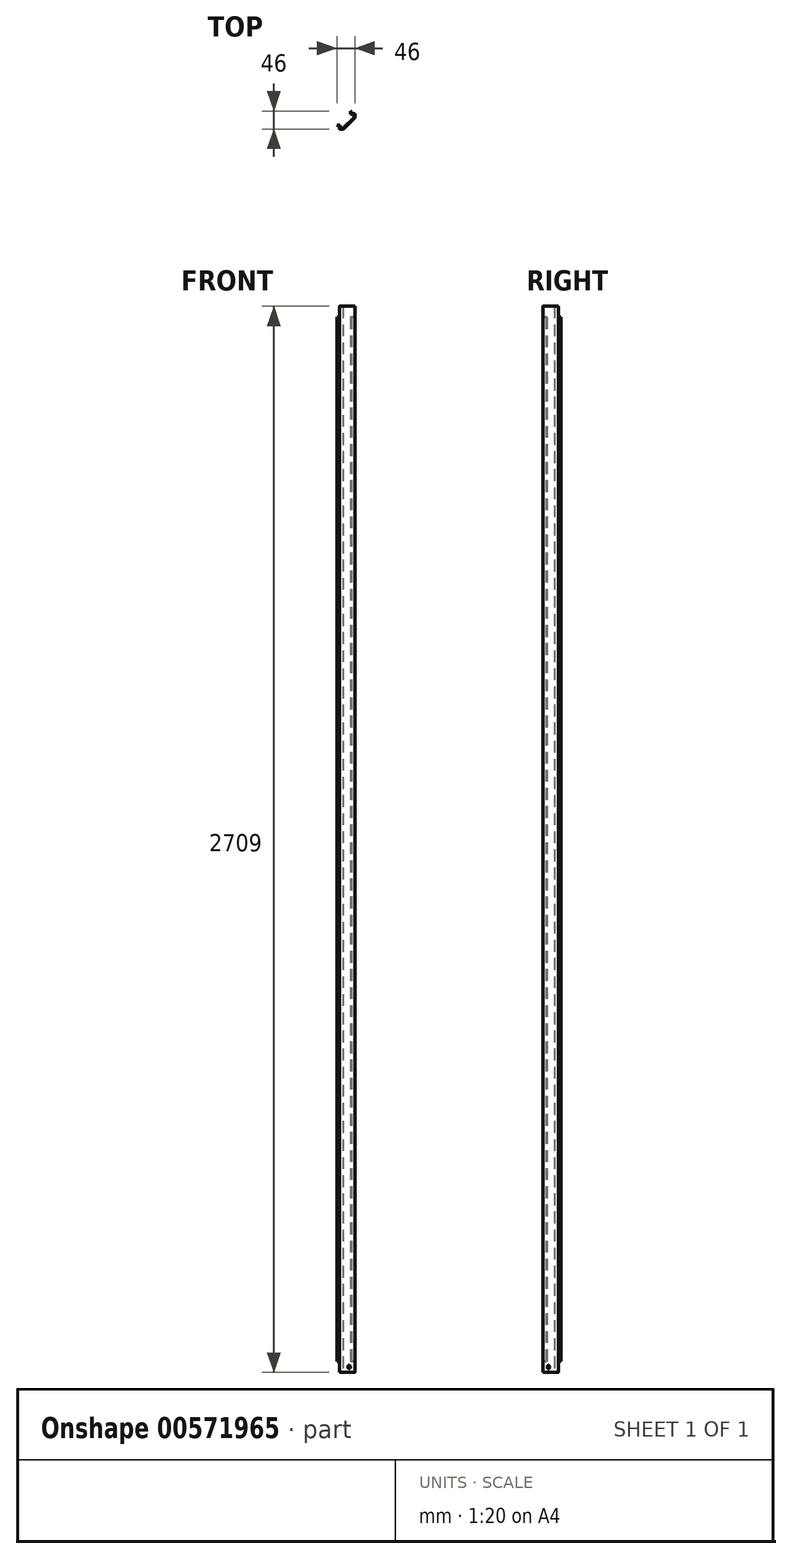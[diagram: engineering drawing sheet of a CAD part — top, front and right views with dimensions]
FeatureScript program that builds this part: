
annotation { "Feature Type Name" : "Feature", "Feature Type Description" : "" }
export const myFeature = defineFeature(function(context is Context, id is Id, definition is map)
    precondition{}
    {
        {
            var Q0;
            Q0=qCreatedBy(makeId("Top.planeOp"),FACE);
            var sketch = newSketch(context, id + "F0", { "sketchPlane" : qUnion([Q0])});
            skLineSegment(sketch, "E0", {"start": v(-68.1, 0) * mm, "end": v(72.16, 0) * mm, "construction": true});
            skLineSegment(sketch, "E1", {"start": v(0, 70.28) * mm, "end": v(0, -61.88) * mm, "construction": true});
            skLineSegment(sketch, "E2.bottom", {"start": v(-19.75, 19.75) * mm, "end": v(19.75, 19.75) * mm, "construction": true});
            skLineSegment(sketch, "E2.top", {"start": v(-19.75, -19.75) * mm, "end": v(19.75, -19.75) * mm, "construction": true});
            skLineSegment(sketch, "E2.left", {"start": v(-19.75, 19.75) * mm, "end": v(-19.75, -19.75) * mm, "construction": true});
            skLineSegment(sketch, "E2.right", {"start": v(19.75, 19.75) * mm, "end": v(19.75, -19.75) * mm, "construction": true});
            skLineSegment(sketch, "E3", {"start": v(-19.75, -19.75) * mm, "end": v(-9.25, -19.75) * mm});
            skLineSegment(sketch, "E4", {"start": v(19.75, 19.75) * mm, "end": v(19.75, 9.25) * mm});
            skLineSegment(sketch, "E5", {"start": v(-9.25, -19.75) * mm, "end": v(19.75, 9.25) * mm});
            skLineSegment(sketch, "E6.0", {"start": v(-19.75, -17.75) * mm, "end": v(-10.08, -17.75) * mm});
            skLineSegment(sketch, "E6.1", {"start": v(-10.08, -17.75) * mm, "end": v(17.75, 10.08) * mm});
            skLineSegment(sketch, "E6.2", {"start": v(17.75, 19.75) * mm, "end": v(17.75, 10.08) * mm});
            skLineSegment(sketch, "E7", {"start": v(-19.75, -19.75) * mm, "end": v(-19.75, -17.75) * mm});
            skLineSegment(sketch, "E8", {"start": v(19.75, 19.75) * mm, "end": v(17.75, 19.75) * mm});
            skSolve(sketch);
        }
        {
            var Q0;
            Q0=qSketchRegion(id+"F0",true);
            extrude(context, id + "F1", {"entities" : qUnion([Q0]), "depth" : 28 * mm});
        }
        {
            var Q0;
            Q0=makeQuery(id+"F1.opExtrude","CAP_FACE",FACE,{"disambiguationData":[OSD([sQuery(id+"F0.wireOp",EDGE,"E3"),sQuery(id+"F0.wireOp",EDGE,"E4"),sQuery(id+"F0.wireOp",EDGE,"E5"),sQuery(id+"F0.wireOp",EDGE,"E6.0"),sQuery(id+"F0.wireOp",EDGE,"E6.1"),sQuery(id+"F0.wireOp",EDGE,"E6.2"),sQuery(id+"F0.wireOp",EDGE,"E7"),sQuery(id+"F0.wireOp",EDGE,"E8")])],"isStart":false});
            var sketch = newSketch(context, id + "F2", { "sketchPlane" : qUnion([Q0])});
            skLineSegment(sketch, "E9.1", {"start": v(-9.25, -19.75) * mm, "end": v(19.75, 9.25) * mm});
            skLineSegment(sketch, "E9.2", {"start": v(19.75, 19.75) * mm, "end": v(19.75, 9.25) * mm});
            skLineSegment(sketch, "E10", {"start": v(19.75, 19.75) * mm, "end": v(11.25, 19.75) * mm});
            skLineSegment(sketch, "E11", {"start": v(17.75, 17.75) * mm, "end": v(17.75, 10.08) * mm});
            skLineSegment(sketch, "E12", {"start": v(17.75, 10.08) * mm, "end": v(16.59, 8.91) * mm});
            skLineSegment(sketch, "E13.left", {"start": v(11.25, 19.75) * mm, "end": v(11.25, 24.25) * mm});
            skLineSegment(sketch, "E14", {"start": v(11.25, 24.25) * mm, "end": v(9.25, 26.25) * mm});
            skLineSegment(sketch, "E15.trimOffspring", {"start": v(16.59, 8.91) * mm, "end": v(-8.91, -16.59) * mm});
            skLineSegment(sketch, "E16.0", {"start": v(9.25, 19.75) * mm, "end": v(9.25, 23.42) * mm});
            skLineSegment(sketch, "E17.0", {"start": v(9.25, 23.42) * mm, "end": v(9.25, 23.42) * mm});
            skLineSegment(sketch, "E18.trimOffspring", {"start": v(9.25, 23.42) * mm, "end": v(9.25, 26.25) * mm});
            skLineSegment(sketch, "E19", {"start": v(0, 0) * mm, "end": v(5.25, -5.25) * mm, "construction": true});
            skLineSegment(sketch, "E20.MirrorCS", {"start": v(-19.75, -9.25) * mm, "end": v(-23.42, -9.25) * mm});
            skLineSegment(sketch, "E21.MirrorCS", {"start": v(-19.75, -11.25) * mm, "end": v(-24.25, -11.25) * mm});
            skLineSegment(sketch, "E22.MirrorCS", {"start": v(-23.42, -9.25) * mm, "end": v(-26.25, -9.25) * mm});
            skLineSegment(sketch, "E23.MirrorCS", {"start": v(-19.75, -19.75) * mm, "end": v(-9.25, -19.75) * mm});
            skLineSegment(sketch, "E24.MirrorCS", {"start": v(-10.08, -17.75) * mm, "end": v(-8.91, -16.59) * mm});
            skLineSegment(sketch, "E25.MirrorCS", {"start": v(-24.25, -11.25) * mm, "end": v(-26.25, -9.25) * mm});
            skLineSegment(sketch, "E26.MirrorCS", {"start": v(-17.75, -17.75) * mm, "end": v(-10.08, -17.75) * mm});
            skLineSegment(sketch, "E27.MirrorCS", {"start": v(-23.42, -9.25) * mm, "end": v(-23.42, -9.25) * mm});
            skLineSegment(sketch, "E28.MirrorCS", {"start": v(-19.75, -19.75) * mm, "end": v(-19.75, -11.25) * mm});
            skLineSegment(sketch, "E29.trimOffspring", {"start": v(-8.91, -16.59) * mm, "end": v(-10.08, -17.75) * mm});
            skLineSegment(sketch, "E30", {"start": v(9.25, 19.75) * mm, "end": v(9.25, 17.75) * mm});
            skLineSegment(sketch, "E31", {"start": v(9.25, 17.75) * mm, "end": v(17.75, 17.75) * mm});
            skLineSegment(sketch, "E32", {"start": v(-19.75, -9.25) * mm, "end": v(-17.75, -9.25) * mm});
            skLineSegment(sketch, "E33", {"start": v(-17.75, -9.25) * mm, "end": v(-17.75, -17.75) * mm});
            skSolve(sketch);
        }
        {
            var Q0;
            Q0=qSketchRegion(id+"F2",true);
            extrude(context, id + "F3", {"entities" : qUnion([Q0]), "operationType" : NewBodyOperationType.ADD, "depth" : 2653 * mm, "offsetDistance" : 25 * mm});
        }
        {
            var Q0;
            Q0=makeQuery(id+"F3.opExtrude","CAP_FACE",FACE,{"disambiguationData":[OSD([sQuery(id+"F2.wireOp",EDGE,"E9.1"),sQuery(id+"F2.wireOp",EDGE,"E9.2"),sQuery(id+"F2.wireOp",EDGE,"E10"),sQuery(id+"F2.wireOp",EDGE,"E11"),sQuery(id+"F2.wireOp",EDGE,"E12"),sQuery(id+"F2.wireOp",EDGE,"E13.left"),sQuery(id+"F2.wireOp",EDGE,"E14"),sQuery(id+"F2.wireOp",EDGE,"E15.trimOffspring"),sQuery(id+"F2.wireOp",EDGE,"E16.0"),sQuery(id+"F2.wireOp",EDGE,"E17.0"),sQuery(id+"F2.wireOp",EDGE,"E18.trimOffspring"),sQuery(id+"F2.wireOp",EDGE,"E20.MirrorCS"),sQuery(id+"F2.wireOp",EDGE,"E21.MirrorCS"),sQuery(id+"F2.wireOp",EDGE,"E22.MirrorCS"),sQuery(id+"F2.wireOp",EDGE,"E23.MirrorCS"),sQuery(id+"F2.wireOp",EDGE,"E25.MirrorCS"),sQuery(id+"F2.wireOp",EDGE,"E26.MirrorCS"),sQuery(id+"F2.wireOp",EDGE,"E27.MirrorCS"),sQuery(id+"F2.wireOp",EDGE,"E28.MirrorCS"),sQuery(id+"F2.wireOp",EDGE,"E29.trimOffspring"),sQuery(id+"F2.wireOp",EDGE,"E30"),sQuery(id+"F2.wireOp",EDGE,"E31"),sQuery(id+"F2.wireOp",EDGE,"E32"),sQuery(id+"F2.wireOp",EDGE,"E33")])],"isStart":false});
            var sketch = newSketch(context, id + "F4", { "sketchPlane" : qUnion([Q0])});
            skLineSegment(sketch, "E34.0.0", {"start": v(19.75, 19.75) * mm, "end": v(19.75, 9.25) * mm});
            skLineSegment(sketch, "E34.0.1", {"start": v(19.75, 9.25) * mm, "end": v(-9.25, -19.75) * mm});
            skLineSegment(sketch, "E34.0.2", {"start": v(-9.25, -19.75) * mm, "end": v(-19.75, -19.75) * mm});
            skLineSegment(sketch, "E34.0.3", {"start": v(-19.75, -19.75) * mm, "end": v(-19.75, -17.75) * mm});
            skLineSegment(sketch, "E34.0.4", {"start": v(-19.75, -17.75) * mm, "end": v(-10.08, -17.75) * mm});
            skLineSegment(sketch, "E34.0.5", {"start": v(-10.08, -17.75) * mm, "end": v(17.75, 10.08) * mm});
            skLineSegment(sketch, "E34.0.6", {"start": v(17.75, 10.08) * mm, "end": v(17.75, 19.75) * mm});
            skLineSegment(sketch, "E34.0.7", {"start": v(17.75, 19.75) * mm, "end": v(19.75, 19.75) * mm});
            skSolve(sketch);
        }
        {
            var Q0;
            Q0=qSketchRegion(id+"F4",true);
            extrude(context, id + "F5", {"entities" : qUnion([Q0]), "operationType" : NewBodyOperationType.ADD, "depth" : 28 * mm});
        }
        {
            var Q0;
            Q0=makeQuery(id+"F5.boolean.opBoolean","MERGE",EDGE,{"derivedFrom":[makeQuery(id+"F3.boolean.opBoolean","MERGE",EDGE,{"derivedFrom":[makeQuery(id+"F1.opExtrude","SWEPT_EDGE",EDGE,{"disambiguationData":[OSD([sQuery(id+"F0.wireOp",EDGE,"E4"),sQuery(id+"F0.wireOp",EDGE,"E5")])]}),makeQuery(id+"F3.opExtrude","SWEPT_EDGE",EDGE,{"disambiguationData":[OSD([sQuery(id+"F2.wireOp",EDGE,"E9.1"),sQuery(id+"F2.wireOp",EDGE,"E9.2")])]})]}),makeQuery(id+"F5.opExtrude","SWEPT_EDGE",EDGE,{"disambiguationData":[OSD([sQuery(id+"F4.wireOp",EDGE,"E34.0.0"),sQuery(id+"F4.wireOp",EDGE,"E34.0.1")])]})]});
            var Q1;
            Q1=makeQuery(id+"F5.boolean.opBoolean","MERGE",EDGE,{"derivedFrom":[makeQuery(id+"F3.boolean.opBoolean","MERGE",EDGE,{"derivedFrom":[makeQuery(id+"F1.opExtrude","SWEPT_EDGE",EDGE,{"disambiguationData":[OSD([sQuery(id+"F0.wireOp",EDGE,"E3"),sQuery(id+"F0.wireOp",EDGE,"E5")])]}),makeQuery(id+"F3.opExtrude","SWEPT_EDGE",EDGE,{"disambiguationData":[OSD([sQuery(id+"F2.wireOp",EDGE,"E9.1"),sQuery(id+"F2.wireOp",EDGE,"E23.MirrorCS")])]})]}),makeQuery(id+"F5.opExtrude","SWEPT_EDGE",EDGE,{"disambiguationData":[OSD([sQuery(id+"F4.wireOp",EDGE,"E34.0.1"),sQuery(id+"F4.wireOp",EDGE,"E34.0.2")])]})]});
            fillet(context, id + "F6", {"entities" : qUnion([Q0, Q1]), "radius" : 2 * mm, "tangentPropagation" : true, "allowEdgeOverflow" : false});
        }
        {
            var Q0;
            Q0=makeQuery(id+"F5.boolean.opBoolean","MERGE",EDGE,{"derivedFrom":[makeQuery(id+"F3.boolean.opBoolean","MERGE",EDGE,{"derivedFrom":[makeQuery(id+"F1.opExtrude","SWEPT_EDGE",EDGE,{"disambiguationData":[OSD([sQuery(id+"F0.wireOp",EDGE,"E3"),sQuery(id+"F0.wireOp",EDGE,"E7")])]}),makeQuery(id+"F3.opExtrude","SWEPT_EDGE",EDGE,{"disambiguationData":[OSD([sQuery(id+"F2.wireOp",EDGE,"E23.MirrorCS"),sQuery(id+"F2.wireOp",EDGE,"E28.MirrorCS")])]})]}),makeQuery(id+"F5.opExtrude","SWEPT_EDGE",EDGE,{"disambiguationData":[OSD([sQuery(id+"F4.wireOp",EDGE,"E34.0.2"),sQuery(id+"F4.wireOp",EDGE,"E34.0.3")])]})]});
            var Q1;
            Q1=makeQuery(id+"F5.boolean.opBoolean","MERGE",EDGE,{"derivedFrom":[makeQuery(id+"F3.boolean.opBoolean","MERGE",EDGE,{"derivedFrom":[makeQuery(id+"F1.opExtrude","SWEPT_EDGE",EDGE,{"disambiguationData":[OSD([sQuery(id+"F0.wireOp",EDGE,"E4"),sQuery(id+"F0.wireOp",EDGE,"E8")])]}),makeQuery(id+"F3.opExtrude","SWEPT_EDGE",EDGE,{"disambiguationData":[OSD([sQuery(id+"F2.wireOp",EDGE,"E9.2"),sQuery(id+"F2.wireOp",EDGE,"E10")])]})]}),makeQuery(id+"F5.opExtrude","SWEPT_EDGE",EDGE,{"disambiguationData":[OSD([sQuery(id+"F4.wireOp",EDGE,"E34.0.0"),sQuery(id+"F4.wireOp",EDGE,"E34.0.7")])]})]});
            fillet(context, id + "F7", {"entities" : qUnion([Q0, Q1]), "radius" : 1 * mm, "tangentPropagation" : true, "allowEdgeOverflow" : false});
        }
        {
            var Q0;
            Q0=makeQuery(id+"F5.boolean.opBoolean","MERGE",FACE,{"derivedFrom":[makeQuery(id+"F3.boolean.opBoolean","MERGE",FACE,{"derivedFrom":[makeQuery(id+"F1.opExtrude","SWEPT_FACE",FACE,{"disambiguationData":[OSD([sQuery(id+"F0.wireOp",EDGE,"E6.1")])]}),makeQuery(id+"F3.opExtrude","SWEPT_FACE",FACE,{"disambiguationData":[OSD([sQuery(id+"F2.wireOp",EDGE,"E12"),sQuery(id+"F2.wireOp",EDGE,"E15.trimOffspring"),sQuery(id+"F2.wireOp",EDGE,"E29.trimOffspring")])]})]}),makeQuery(id+"F5.opExtrude","SWEPT_FACE",FACE,{"disambiguationData":[OSD([sQuery(id+"F4.wireOp",EDGE,"E34.0.5")])]})]});
            var sketch = newSketch(context, id + "F8", { "sketchPlane" : qUnion([Q0])});
            skLineSegment(sketch, "E35", {"start": v(-26.52, 28) * mm, "end": v(26.52, 28) * mm, "construction": true});
            skLineSegment(sketch, "E36", {"start": v(0, 28) * mm, "end": v(0, 0) * mm, "construction": true});
            skCircle(sketch, "E37", {"center": v(0, 14) * mm, "radius": 4.25 * mm});
            skSolve(sketch);
        }
        {
            var Q0;
            Q0=qSketchRegion(id+"F8",true);
            extrude(context, id + "F9", {"entities" : qUnion([Q0]), "operationType" : NewBodyOperationType.REMOVE, "oppositeDirection" : true, "depth" : 25 * mm, "offsetDistance" : 25 * mm});
        }
    });
